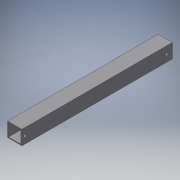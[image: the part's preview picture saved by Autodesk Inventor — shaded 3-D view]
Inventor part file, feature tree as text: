
AUTODESK INVENTOR PART (.ipt)
format: ipt  version: 2018 (Build 220112000, 112)  size: 112,640 bytes
history: native  units: in
note: dims shown in document units (in); Inventor stores cm internally (conversion verified against a paired STEP export)
features: extrude x2, sketch x2
ambient origin geometry x8: Origin, YZ Plane, XZ Plane, XY Plane, X Axis, Y Axis, Z Axis, Center Point
bodies: Solid1 (feature_tree)
feature tree (4):
  extrude  "Extrusion1"  Depth=1.0in
  extrude  "Extrusion2"  Depth=0.065in
  sketch  "Sketch1"  dims[d0=1.0in d1=1.0in]
  sketch  "Sketch2"  dims[d2=0.065in d3=0.065in d4=10.5in d5=0.0in d6=9.878in d7=0.2in d8=0.2in d11=0.1in d12=0.0in d15=0.5in d16=0.5in]
